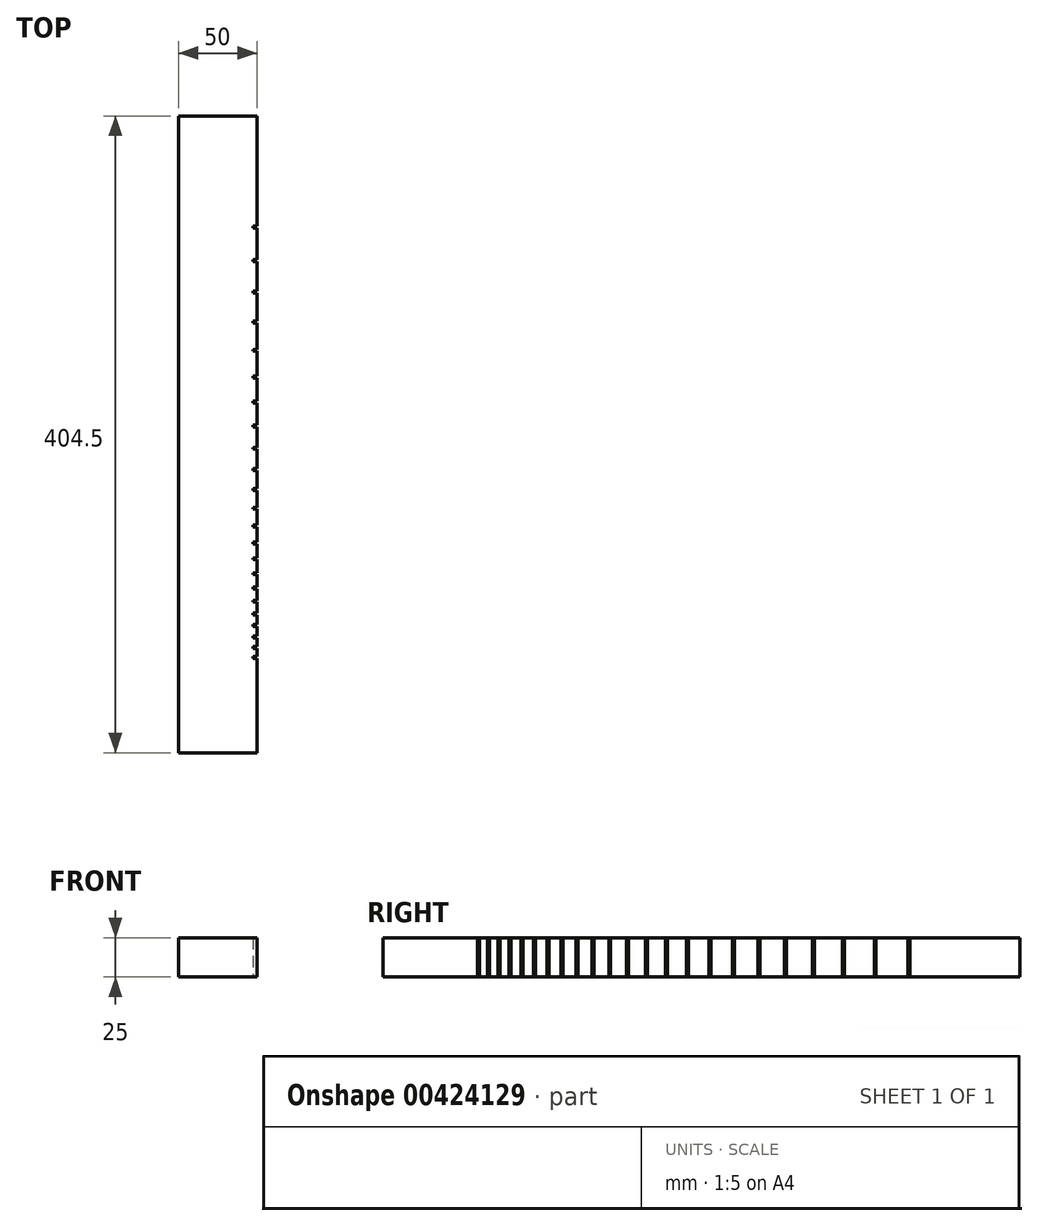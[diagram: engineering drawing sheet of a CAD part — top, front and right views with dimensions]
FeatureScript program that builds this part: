
annotation { "Feature Type Name" : "Feature", "Feature Type Description" : "" }
export const myFeature = defineFeature(function(context is Context, id is Id, definition is map)
    precondition{}
    {
        {
            var Q0;
            Q0=qCreatedBy(makeId("Top.planeOp"),FACE);
            var sketch = newSketch(context, id + "F0", { "sketchPlane" : qUnion([Q0])});
            skLineSegment(sketch, "E0", {"start": v(0, 0) * mm, "end": v(0, -20) * mm});
            skLineSegment(sketch, "E1", {"start": v(0, -20) * mm, "end": v(-2.5, -20) * mm});
            skLineSegment(sketch, "E2", {"start": v(-2.5, -20) * mm, "end": v(-2.5, -21.2) * mm});
            skLineSegment(sketch, "E3", {"start": v(-2.5, -21.2) * mm, "end": v(0, -21.2) * mm});
            skLineSegment(sketch, "E4", {"start": v(0, -21.2) * mm, "end": v(0, -41.3) * mm});
            skLineSegment(sketch, "E5", {"start": v(0, -41.3) * mm, "end": v(-2.5, -41.3) * mm});
            skLineSegment(sketch, "E6", {"start": v(-2.5, -41.3) * mm, "end": v(-2.5, -42.5) * mm});
            skLineSegment(sketch, "E7", {"start": v(-2.5, -42.5) * mm, "end": v(0, -42.5) * mm});
            skLineSegment(sketch, "E8", {"start": v(0, -42.5) * mm, "end": v(0, -61.4) * mm});
            skLineSegment(sketch, "E9", {"start": v(0, -61.4) * mm, "end": v(-2.5, -61.4) * mm});
            skLineSegment(sketch, "E10", {"start": v(-2.5, -61.4) * mm, "end": v(-2.5, -62.6) * mm});
            skLineSegment(sketch, "E11", {"start": v(-2.5, -62.6) * mm, "end": v(0, -62.6) * mm});
            skLineSegment(sketch, "E12", {"start": v(0, -62.6) * mm, "end": v(0, -80.4) * mm});
            skLineSegment(sketch, "E13", {"start": v(0, -80.4) * mm, "end": v(-2.5, -80.4) * mm});
            skLineSegment(sketch, "E14", {"start": v(-2.5, -80.4) * mm, "end": v(-2.5, -81.6) * mm});
            skLineSegment(sketch, "E15", {"start": v(-2.5, -81.6) * mm, "end": v(0, -81.6) * mm});
            skLineSegment(sketch, "E16", {"start": v(0, -81.6) * mm, "end": v(0, -98.3) * mm});
            skLineSegment(sketch, "E17", {"start": v(0, -98.3) * mm, "end": v(-2.5, -98.3) * mm});
            skLineSegment(sketch, "E18", {"start": v(-2.5, -98.3) * mm, "end": v(-2.5, -99.5) * mm});
            skLineSegment(sketch, "E19", {"start": v(-2.5, -99.5) * mm, "end": v(0, -99.5) * mm});
            skLineSegment(sketch, "E20", {"start": v(0, -99.5) * mm, "end": v(0, -115.2) * mm});
            skLineSegment(sketch, "E21", {"start": v(0, -131.2) * mm, "end": v(-2.5, -131.2) * mm});
            skLineSegment(sketch, "E22", {"start": v(-2.5, -131.2) * mm, "end": v(-2.5, -132.4) * mm});
            skLineSegment(sketch, "E23", {"start": v(-2.5, -132.4) * mm, "end": v(0, -132.4) * mm});
            skLineSegment(sketch, "E24", {"start": v(0, -132.4) * mm, "end": v(0, -146.3) * mm});
            skLineSegment(sketch, "E25", {"start": v(0, -146.3) * mm, "end": v(-2.5, -146.3) * mm});
            skLineSegment(sketch, "E26", {"start": v(-2.5, -146.3) * mm, "end": v(-2.5, -147.5) * mm});
            skLineSegment(sketch, "E27", {"start": v(-2.5, -147.5) * mm, "end": v(0, -147.5) * mm});
            skLineSegment(sketch, "E28", {"start": v(0, -147.5) * mm, "end": v(0, -160.5) * mm});
            skLineSegment(sketch, "E29", {"start": v(0, -160.5) * mm, "end": v(-2.5, -160.5) * mm});
            skLineSegment(sketch, "E30", {"start": v(-2.5, -160.5) * mm, "end": v(-2.5, -161.7) * mm});
            skLineSegment(sketch, "E31", {"start": v(-2.5, -161.7) * mm, "end": v(0, -161.7) * mm});
            skLineSegment(sketch, "E32", {"start": v(0, -161.7) * mm, "end": v(0, -173.9) * mm});
            skLineSegment(sketch, "E33", {"start": v(0, -173.9) * mm, "end": v(-2.5, -173.9) * mm});
            skLineSegment(sketch, "E34", {"start": v(-2.5, -173.9) * mm, "end": v(-2.5, -175.1) * mm});
            skLineSegment(sketch, "E35", {"start": v(-2.5, -175.1) * mm, "end": v(0, -175.1) * mm});
            skLineSegment(sketch, "E36", {"start": v(0, -175.1) * mm, "end": v(0, -186.6) * mm});
            skLineSegment(sketch, "E37", {"start": v(0, -186.6) * mm, "end": v(-2.5, -186.6) * mm});
            skLineSegment(sketch, "E38", {"start": v(-2.5, -186.6) * mm, "end": v(-2.5, -187.8) * mm});
            skLineSegment(sketch, "E39", {"start": v(-2.5, -187.8) * mm, "end": v(0, -187.8) * mm});
            skLineSegment(sketch, "E40", {"start": v(0, -187.8) * mm, "end": v(0, -198.6) * mm});
            skLineSegment(sketch, "E41", {"start": v(0, -198.6) * mm, "end": v(-2.5, -198.6) * mm});
            skLineSegment(sketch, "E42", {"start": v(-2.5, -198.6) * mm, "end": v(-2.5, -199.8) * mm});
            skLineSegment(sketch, "E43", {"start": v(-2.5, -199.8) * mm, "end": v(0, -199.8) * mm});
            skLineSegment(sketch, "E44", {"start": v(0, -199.8) * mm, "end": v(0, -209.9) * mm});
            skLineSegment(sketch, "E45", {"start": v(0, -209.9) * mm, "end": v(-2.5, -209.9) * mm});
            skLineSegment(sketch, "E46", {"start": v(-2.5, -209.9) * mm, "end": v(-2.5, -211.1) * mm});
            skLineSegment(sketch, "E47", {"start": v(-2.5, -211.1) * mm, "end": v(0, -211.1) * mm});
            skLineSegment(sketch, "E48", {"start": v(0, -211.1) * mm, "end": v(0, -220.6) * mm});
            skLineSegment(sketch, "E49", {"start": v(0, -220.6) * mm, "end": v(-2.5, -220.6) * mm});
            skLineSegment(sketch, "E50", {"start": v(-2.5, -220.6) * mm, "end": v(-2.5, -221.8) * mm});
            skLineSegment(sketch, "E51", {"start": v(-2.5, -221.8) * mm, "end": v(0, -221.8) * mm});
            skLineSegment(sketch, "E52", {"start": v(0, -221.8) * mm, "end": v(0, -230.7) * mm});
            skLineSegment(sketch, "E53", {"start": v(0, -230.7) * mm, "end": v(-2.5, -230.7) * mm});
            skLineSegment(sketch, "E54", {"start": v(-2.5, -230.7) * mm, "end": v(-2.5, -231.9) * mm});
            skLineSegment(sketch, "E55", {"start": v(-2.5, -231.9) * mm, "end": v(0, -231.9) * mm});
            skLineSegment(sketch, "E56", {"start": v(0, -231.9) * mm, "end": v(0, -240.2) * mm});
            skLineSegment(sketch, "E57", {"start": v(0, -240.2) * mm, "end": v(-2.5, -240.2) * mm});
            skLineSegment(sketch, "E58", {"start": v(-2.5, -240.2) * mm, "end": v(-2.5, -241.4) * mm});
            skLineSegment(sketch, "E59", {"start": v(-2.5, -241.4) * mm, "end": v(0, -241.4) * mm});
            skLineSegment(sketch, "E60", {"start": v(0, -241.4) * mm, "end": v(0, -249.2) * mm});
            skLineSegment(sketch, "E61", {"start": v(0, -249.2) * mm, "end": v(-2.5, -249.2) * mm});
            skLineSegment(sketch, "E62", {"start": v(-2.5, -249.2) * mm, "end": v(-2.5, -250.4) * mm});
            skLineSegment(sketch, "E63", {"start": v(-2.5, -250.4) * mm, "end": v(0, -250.4) * mm});
            skLineSegment(sketch, "E64", {"start": v(0, -250.4) * mm, "end": v(0, -257.7) * mm});
            skLineSegment(sketch, "E65", {"start": v(0, -257.7) * mm, "end": v(-2.5, -257.7) * mm});
            skLineSegment(sketch, "E66", {"start": v(-2.5, -257.7) * mm, "end": v(-2.5, -258.9) * mm});
            skLineSegment(sketch, "E67", {"start": v(-2.5, -258.9) * mm, "end": v(0, -258.9) * mm});
            skLineSegment(sketch, "E68", {"start": v(0, -258.9) * mm, "end": v(0, -265.7) * mm});
            skLineSegment(sketch, "E69", {"start": v(0, -265.7) * mm, "end": v(-2.5, -265.7) * mm});
            skLineSegment(sketch, "E70", {"start": v(-2.5, -265.7) * mm, "end": v(-2.5, -266.9) * mm});
            skLineSegment(sketch, "E71", {"start": v(-2.5, -266.9) * mm, "end": v(0, -266.9) * mm});
            skLineSegment(sketch, "E72", {"start": v(0, -266.9) * mm, "end": v(0, -273.2) * mm});
            skLineSegment(sketch, "E73", {"start": v(0, -273.2) * mm, "end": v(-2.5, -273.2) * mm});
            skLineSegment(sketch, "E74", {"start": v(-2.5, -273.2) * mm, "end": v(-2.5, -274.4) * mm});
            skLineSegment(sketch, "E75", {"start": v(-2.5, -274.4) * mm, "end": v(0, -274.4) * mm});
            skLineSegment(sketch, "E76", {"start": v(0, -274.4) * mm, "end": v(0, -280.3) * mm});
            skLineSegment(sketch, "E77", {"start": v(0, -280.3) * mm, "end": v(-2.5, -280.3) * mm});
            skLineSegment(sketch, "E78", {"start": v(-2.5, -280.3) * mm, "end": v(-2.5, -281.5) * mm});
            skLineSegment(sketch, "E79", {"start": v(-2.5, -281.5) * mm, "end": v(0, -281.5) * mm});
            skLineSegment(sketch, "E80", {"start": v(0, -281.5) * mm, "end": v(0, -287) * mm});
            skLineSegment(sketch, "E81", {"start": v(0, -287) * mm, "end": v(-2.5, -287) * mm});
            skLineSegment(sketch, "E82", {"start": v(-2.5, -287) * mm, "end": v(-2.5, -288.2) * mm});
            skLineSegment(sketch, "E83", {"start": v(-2.5, -288.2) * mm, "end": v(0, -288.2) * mm});
            skLineSegment(sketch, "E84", {"start": v(0, -288.2) * mm, "end": v(0, -293.3) * mm});
            skLineSegment(sketch, "E85", {"start": v(0, -293.3) * mm, "end": v(-2.5, -293.3) * mm});
            skLineSegment(sketch, "E86", {"start": v(-2.5, -293.3) * mm, "end": v(-2.5, -294.5) * mm});
            skLineSegment(sketch, "E87", {"start": v(-2.5, -294.5) * mm, "end": v(0, -294.5) * mm});
            skLineSegment(sketch, "E88", {"start": v(0, -294.5) * mm, "end": v(0, -304.5) * mm});
            skLineSegment(sketch, "E89", {"start": v(0, -304.5) * mm, "end": v(-50, -304.5) * mm});
            skLineSegment(sketch, "E90", {"start": v(-50, -304.5) * mm, "end": v(-50, 0) * mm});
            skLineSegment(sketch, "E91", {"start": v(-50, 0) * mm, "end": v(0, 0) * mm});
            skLineSegment(sketch, "E92", {"start": v(0, -131.2) * mm, "end": v(0, -116.4) * mm});
            skLineSegment(sketch, "E93", {"start": v(0, -116.4) * mm, "end": v(-2.5, -116.4) * mm});
            skLineSegment(sketch, "E94", {"start": v(-2.5, -116.4) * mm, "end": v(-2.5, -115.2) * mm});
            skLineSegment(sketch, "E95", {"start": v(-2.5, -115.2) * mm, "end": v(0, -115.2) * mm});
            skLineSegment(sketch, "E96.trimOffspring", {"start": v(0, -116.4) * mm, "end": v(0, -131.2) * mm});
            skSolve(sketch);
        }
        {
            var Q0;
            Q0=makeQuery(id+"F0.imprint","IMPRINT",FACE,{"disambiguationData":[TD([[makeQuery(id+"F0.imprint","IMPRINT",EDGE,{"derivedFrom":sQuery(id+"F0.wireOp",EDGE,"E0")}),-1.0]])]});
            extrude(context, id + "F1", {"entities" : qUnion([Q0]), "depth" : 25 * mm});
        }
        {
            var Q0;
            Q0=makeQuery(id+"F1.opExtrude","SWEPT_FACE",FACE,{"disambiguationData":[OSD([sQuery(id+"F0.wireOp",EDGE,"E89")])]});
            var sketch = newSketch(context, id + "F2", { "sketchPlane" : qUnion([Q0])});
            skLineSegment(sketch, "E97.0", {"start": v(-50, 0) * mm, "end": v(0, 0) * mm});
            skLineSegment(sketch, "E97.1", {"start": v(-50, 25) * mm, "end": v(-50, 0) * mm});
            skLineSegment(sketch, "E97.2", {"start": v(0, 25) * mm, "end": v(-50, 25) * mm});
            skLineSegment(sketch, "E97.3", {"start": v(0, 0) * mm, "end": v(0, 25) * mm});
            skSolve(sketch);
        }
        {
            var Q0;
            Q0 = qSketchRegion(id + "F2", true);
            extrude(context, id + "F3", {"entities" : qUnion([Q0]), "operationType" : NewBodyOperationType.ADD, "depth" : 50 * mm});
        }
        {
            var Q0;
            Q0=makeQuery(id+"F1.opExtrude","SWEPT_FACE",FACE,{"disambiguationData":[OSD([sQuery(id+"F0.wireOp",EDGE,"E91")])]});
            var sketch = newSketch(context, id + "F4", { "sketchPlane" : qUnion([Q0])});
            skLineSegment(sketch, "E98.0", {"start": v(0, 0) * mm, "end": v(50, 0) * mm});
            skLineSegment(sketch, "E98.1", {"start": v(0, 25) * mm, "end": v(0, 0) * mm});
            skLineSegment(sketch, "E98.2", {"start": v(50, 25) * mm, "end": v(0, 25) * mm});
            skLineSegment(sketch, "E98.3", {"start": v(50, 0) * mm, "end": v(50, 25) * mm});
            skSolve(sketch);
        }
        {
            var Q0;
            Q0 = qSketchRegion(id + "F4", true);
            extrude(context, id + "F5", {"entities" : qUnion([Q0]), "operationType" : NewBodyOperationType.ADD, "depth" : 50 * mm});
        }
    });
